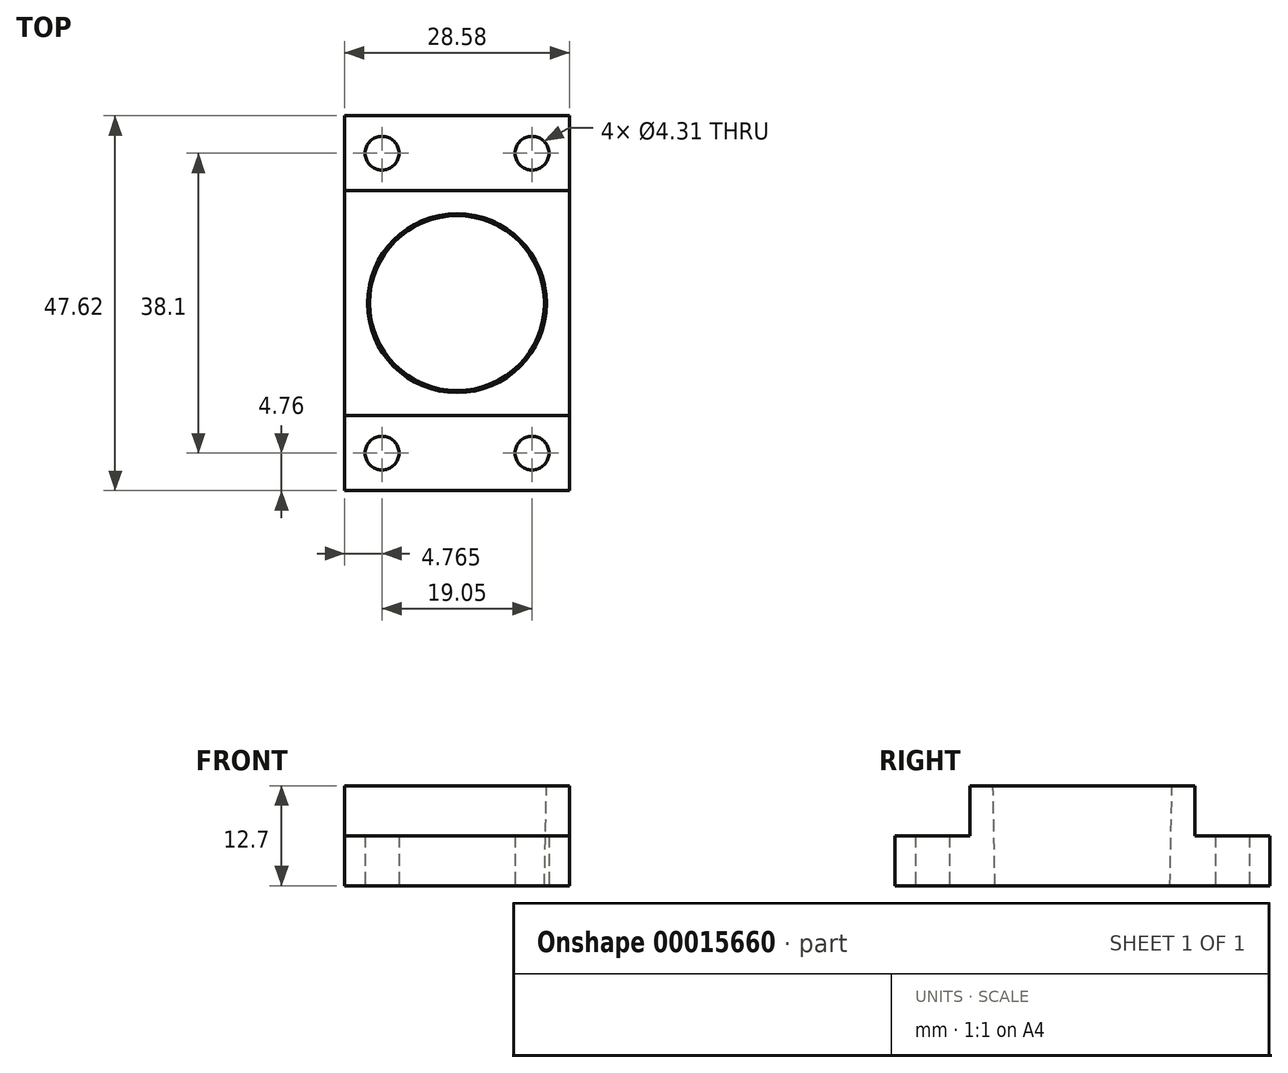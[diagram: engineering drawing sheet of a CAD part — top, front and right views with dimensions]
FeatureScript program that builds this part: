
annotation { "Feature Type Name" : "Feature", "Feature Type Description" : "" }
export const myFeature = defineFeature(function(context is Context, id is Id, definition is map)
    precondition{}
    {
        {
            var Q0;
            Q0=qCreatedBy(makeId("Top.planeOp"),FACE);
            var sketch = newSketch(context, id + "F0", { "sketchPlane" : qUnion([Q0])});
            skLineSegment(sketch, "E0.bottom", {"start": v(-14.29, -23.81) * mm, "end": v(14.29, -23.81) * mm});
            skLineSegment(sketch, "E0.top", {"start": v(-14.29, 23.81) * mm, "end": v(14.29, 23.81) * mm});
            skLineSegment(sketch, "E0.left", {"start": v(-14.29, -23.81) * mm, "end": v(-14.29, 23.81) * mm});
            skLineSegment(sketch, "E0.right", {"start": v(14.29, -23.81) * mm, "end": v(14.29, 23.81) * mm});
            skPoint(sketch, "E0.middle", {"position": v(0, 0) * mm});
            skLineSegment(sketch, "E1.bottom", {"start": v(-9.53, -19.05) * mm, "end": v(9.53, -19.05) * mm, "construction": true});
            skLineSegment(sketch, "E1.top", {"start": v(-9.53, 19.05) * mm, "end": v(9.53, 19.05) * mm, "construction": true});
            skLineSegment(sketch, "E1.left", {"start": v(-9.53, -19.05) * mm, "end": v(-9.53, 19.05) * mm, "construction": true});
            skLineSegment(sketch, "E1.right", {"start": v(9.53, -19.05) * mm, "end": v(9.53, 19.05) * mm, "construction": true});
            skLineSegment(sketch, "E2.bottom", {"start": v(-9.53, -19.05) * mm, "end": v(-14.29, -19.05) * mm, "construction": true});
            skLineSegment(sketch, "E2.left", {"start": v(-9.53, -19.05) * mm, "end": v(-9.53, -23.81) * mm, "construction": true});
            skCircle(sketch, "E3", {"center": v(-9.53, 19.05) * mm, "radius": 2.15 * mm});
            skCircle(sketch, "E4", {"center": v(9.53, 19.05) * mm, "radius": 2.15 * mm});
            skCircle(sketch, "E5", {"center": v(0, 0) * mm, "radius": 11.11 * mm});
            skCircle(sketch, "E6", {"center": v(9.53, -19.05) * mm, "radius": 2.15 * mm});
            skCircle(sketch, "E7", {"center": v(-9.53, -19.05) * mm, "radius": 2.15 * mm});
            skSolve(sketch);
        }
        {
            var Q0;
            Q0 = qSketchRegion(id + "F0", true);
            extrude(context, id + "F1", {"entities" : qUnion([Q0]), "depth" : 6.35 * mm});
        }
        {
            var Q0;
            Q0=makeQuery(id+"F1.opExtrude","CAP_FACE",FACE,{"disambiguationData":[OSD([sQuery(id+"F0.wireOp",EDGE,"E0.bottom"),sQuery(id+"F0.wireOp",EDGE,"E0.top"),sQuery(id+"F0.wireOp",EDGE,"E0.left"),sQuery(id+"F0.wireOp",EDGE,"E0.right"),sQuery(id+"F0.wireOp",EDGE,"E3"),sQuery(id+"F0.wireOp",EDGE,"E4"),sQuery(id+"F0.wireOp",EDGE,"E5"),sQuery(id+"F0.wireOp",EDGE,"E6"),sQuery(id+"F0.wireOp",EDGE,"E7")])],"isStart":false});
            var sketch = newSketch(context, id + "F2", { "sketchPlane" : qUnion([Q0])});
            skCircle(sketch, "E8", {"center": v(0, 0) * mm, "radius": 11.11 * mm});
            skLineSegment(sketch, "E9.bottom", {"start": v(-14.29, 14.29) * mm, "end": v(14.29, 14.29) * mm});
            skLineSegment(sketch, "E9.top", {"start": v(-14.29, -14.29) * mm, "end": v(14.29, -14.29) * mm});
            skLineSegment(sketch, "E9.left", {"start": v(-14.29, 14.29) * mm, "end": v(-14.29, -14.29) * mm});
            skLineSegment(sketch, "E9.right", {"start": v(14.29, 14.29) * mm, "end": v(14.29, -14.29) * mm});
            skSolve(sketch);
        }
        {
            var Q0;
            Q0 = qSketchRegion(id + "F2", true);
            extrude(context, id + "F3", {"entities" : qUnion([Q0]), "operationType" : NewBodyOperationType.ADD, "depth" : 6.35 * mm});
        }
        {
            var Q0;
            Q0=makeQuery(id+"F3.opExtrude","CAP_EDGE",EDGE,{"disambiguationData":[OSD([sQuery(id+"F2.wireOp",EDGE,"E8")])],"isStart":false});
            chamfer(context, id + "F4", {"entities" : qUnion([Q0]), "chamferType" : ChamferType.TWO_OFFSETS, "width1" : 12.7 * mm, "oppositeDirection" : false, "width2" : 0.25 * mm, "tangentPropagation" : true});
        }
    });
